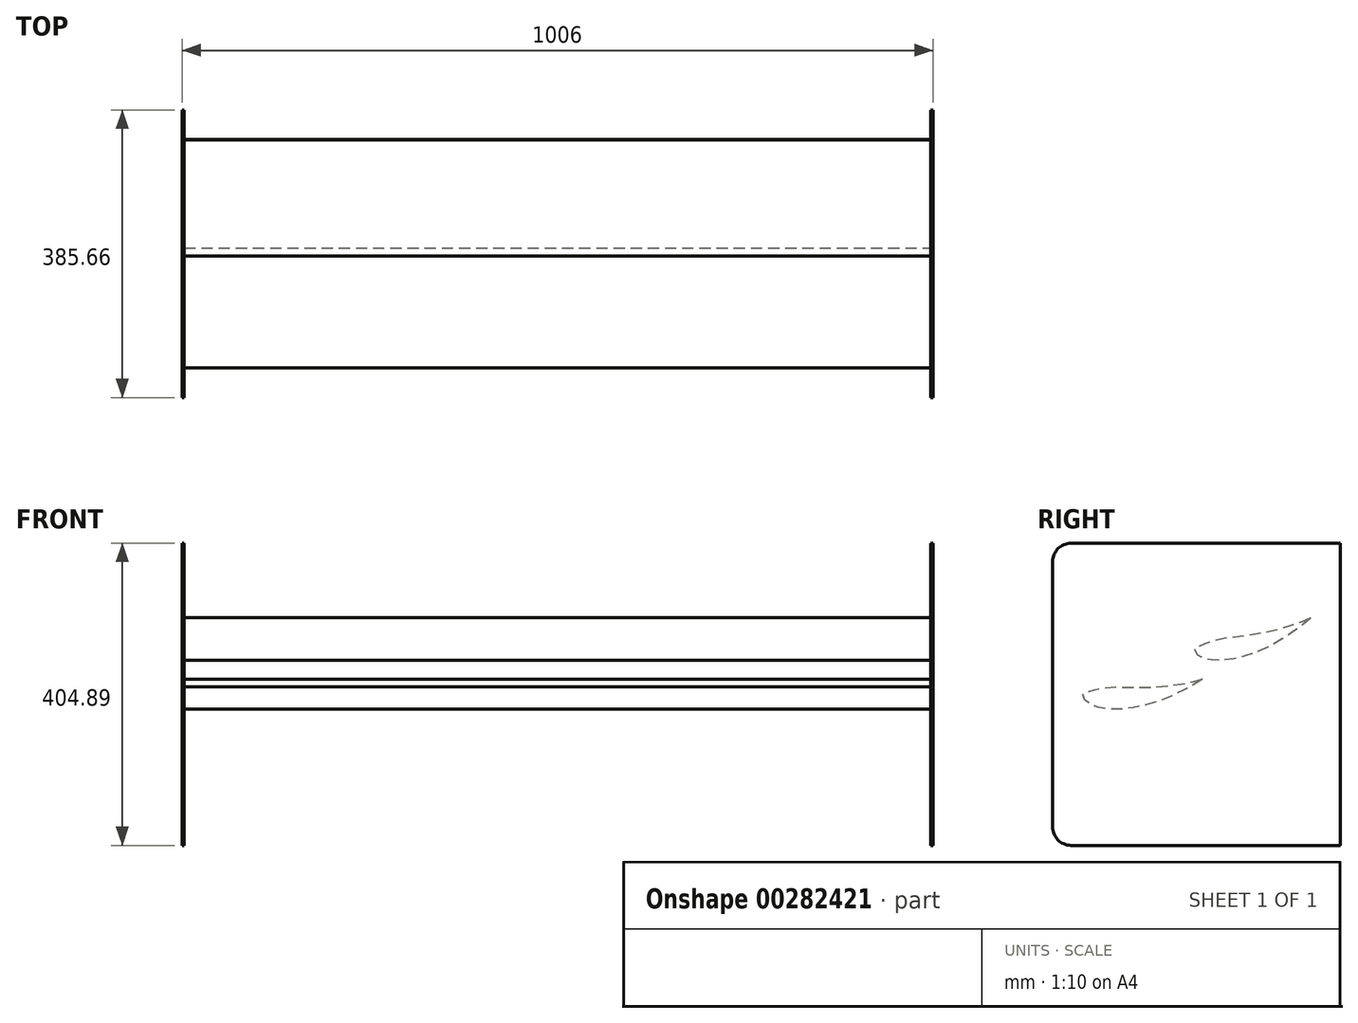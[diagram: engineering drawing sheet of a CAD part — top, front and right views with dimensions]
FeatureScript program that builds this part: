
annotation { "Feature Type Name" : "Feature", "Feature Type Description" : "" }
export const myFeature = defineFeature(function(context is Context, id is Id, definition is map)
    precondition{}
    {
        {
            var Q0;
            Q0=qCreatedBy(makeId("Right.planeOp"),FACE);
            var sketch = newSketch(context, id + "F0", { "sketchPlane" : qUnion([Q0])});
            skPoint(sketch, "E0", {"position": v(1.78, 4.63) * mm});
            skPoint(sketch, "E1", {"position": v(3.68, 7) * mm});
            skPoint(sketch, "E2", {"position": v(7.54, 10.53) * mm});
            skPoint(sketch, "E3", {"position": v(15.35, 15.89) * mm});
            skPoint(sketch, "E4", {"position": v(11.42, 13.57) * mm});
            skPoint(sketch, "E5", {"position": v(23.27, 19.3) * mm});
            skPoint(sketch, "E6", {"position": v(0, 0) * mm});
            skPoint(sketch, "E7", {"position": v(31.25, 21.57) * mm});
            skPoint(sketch, "E8", {"position": v(63.47, 24.86) * mm});
            skPoint(sketch, "E9", {"position": v(47.3, 24.4) * mm});
            skPoint(sketch, "E10", {"position": v(79.72, 23.95) * mm});
            skPoint(sketch, "E11", {"position": v(96.04, 21.74) * mm});
            skPoint(sketch, "E12", {"position": v(112.45, 17.84) * mm});
            skPoint(sketch, "E13", {"position": v(128.9, 13.21) * mm});
            skPoint(sketch, "E14", {"position": v(145.4, 7.3) * mm});
            skPoint(sketch, "E15", {"position": v(153.7, 3.82) * mm});
            skPoint(sketch, "E16", {"position": v(162, 0.24) * mm});
            skPoint(sketch, "E17", {"position": v(162, -0.24) * mm});
            skPoint(sketch, "E18", {"position": v(153.85, 0.94) * mm});
            skPoint(sketch, "E19", {"position": v(129.47, 2.44) * mm});
            skPoint(sketch, "E20", {"position": v(113.27, 2.42) * mm});
            skPoint(sketch, "E21", {"position": v(97.12, 1.47) * mm});
            skPoint(sketch, "E22", {"position": v(81.03, -0.52) * mm});
            skPoint(sketch, "E23", {"position": v(64.96, -2.92) * mm});
            skPoint(sketch, "E24", {"position": v(48.9, -5.48) * mm});
            skPoint(sketch, "E25", {"position": v(32.77, -7) * mm});
            skPoint(sketch, "E26", {"position": v(24.67, -6.94) * mm});
            skPoint(sketch, "E27", {"position": v(16.54, -6.32) * mm});
            skPoint(sketch, "E28", {"position": v(12.46, -5.77) * mm});
            skPoint(sketch, "E29", {"position": v(8.36, -4.82) * mm});
            skPoint(sketch, "E30", {"position": v(4.25, -3.66) * mm});
            skPoint(sketch, "E31", {"position": v(2.17, -2.72) * mm});
            skPoint(sketch, "E32", {"position": v(145.7, 1.72) * mm});
            skFitSpline(sketch, "E33", {"points": [v(162, 0.24) * mm, v(153.7, 3.82) * mm, v(145.4, 7.3) * mm, v(128.9, 13.21) * mm, v(112.45, 17.84) * mm, v(96.04, 21.74) * mm, v(79.72, 23.95) * mm, v(63.47, 24.86) * mm, v(47.3, 24.4) * mm, v(31.25, 21.57) * mm, v(23.27, 19.3) * mm, v(15.35, 15.89) * mm, v(11.42, 13.57) * mm, v(7.54, 10.53) * mm, v(3.68, 7) * mm, v(1.78, 4.63) * mm, v(0, 0) * mm, v(2.17, -2.72) * mm, v(4.25, -3.66) * mm, v(8.36, -4.82) * mm, v(12.46, -5.77) * mm, v(16.54, -6.32) * mm, v(24.67, -6.94) * mm, v(32.77, -7) * mm, v(48.9, -5.48) * mm, v(64.96, -2.92) * mm, v(81.03, -0.52) * mm, v(97.12, 1.47) * mm, v(113.27, 2.42) * mm, v(129.47, 2.44) * mm, v(145.7, 1.72) * mm, v(153.85, 0.94) * mm, v(162, -0.24) * mm], "startDerivative": vector(-283.63, 121.8) * mm, "endDerivative": vector(291.37, -44.72) * mm});
            skLineSegment(sketch, "E34", {"start": v(162, 0.24) * mm, "end": v(162, -0.24) * mm});
            skSolve(sketch);
        }
        {
            var Q0;
            Q0=makeQuery(id+"F0.imprint","IMPRINT",FACE,{"disambiguationData":[TD([[makeQuery(id+"F0.imprint","IMPRINT",EDGE,{"derivedFrom":sQuery(id+"F0.wireOp",EDGE,"E33")}),1.0]])]});
            extrude(context, id + "F1", {"entities" : qUnion([Q0]), "endBound" : BoundingType.SYMMETRIC, "depth" : 1000 * mm});
        }
        {
            var Q0;
            Q0=qCreatedBy(makeId("Top.planeOp"),FACE);
            var sketch = newSketch(context, id + "F2", { "sketchPlane" : qUnion([Q0])});
            skLineSegment(sketch, "E35", {"start": v(0, 0) * mm, "end": v(0, 212.68) * mm});
            skSolve(sketch);
        }
        {
            var Q0;
            Q0=makeQuery(id+"F1.opExtrude","SWEPT_BODY",BODY,{"disambiguationData":[OSD([sQuery(id+"F0.wireOp",EDGE,"E33"),sQuery(id+"F0.wireOp",EDGE,"E34")])]});
            var Q1;
            Q1=sQuery(id+"F2.wireOp",EDGE,"E35");
            transform(context, id + "F3", {"entities" : qUnion([Q0]), "transformType" : TransformType.ROTATION, "transformAxis" : qUnion([Q1]), "angle" : 180 * degree, "makeCopy" : false});
        }
        {
            var Q0;
            Q0=qCreatedBy(makeId("Top.planeOp"),FACE);
            var sketch = newSketch(context, id + "F4", { "sketchPlane" : qUnion([Q0])});
            skLineSegment(sketch, "E36", {"start": v(-76.15, 0) * mm, "end": v(75.87, 0) * mm});
            skSolve(sketch);
        }
        {
            var Q0;
            Q0=makeQuery(id+"F1.opExtrude","SWEPT_BODY",BODY,{"disambiguationData":[OSD([sQuery(id+"F0.wireOp",EDGE,"E33"),sQuery(id+"F0.wireOp",EDGE,"E34")])]});
            var Q1;
            Q1=sQuery(id+"F4.wireOp",EDGE,"E36");
            transform(context, id + "F5", {"entities" : qUnion([Q0]), "transformType" : TransformType.ROTATION, "transformAxis" : qUnion([Q1]), "angle" : 8 * degree, "makeCopy" : false});
        }
        {
            var Q0;
            Q0=makeQuery(id+"F1.opExtrude","SWEPT_BODY",BODY,{"disambiguationData":[OSD([sQuery(id+"F0.wireOp",EDGE,"E33"),sQuery(id+"F0.wireOp",EDGE,"E34")])]});
            var Q1;
            Q1=sQuery(id+"F4.wireOp",EDGE,"E36");
            transform(context, id + "F6", {"entities" : qUnion([Q0]), "transformType" : TransformType.ROTATION, "transformAxis" : qUnion([Q1]), "angle" : 8 * degree, "makeCopy" : true});
        }
        {
            var Q0;
            Q0=makeQuery(id+"F6.opPattern","COPY",BODY,{"derivedFrom":makeQuery(id+"F1.opExtrude","SWEPT_BODY",BODY,{"disambiguationData":[OSD([sQuery(id+"F0.wireOp",EDGE,"E33"),sQuery(id+"F0.wireOp",EDGE,"E34")])]}),"instanceName":"1"});
            transform(context, id + "F7", {"entities" : qUnion([Q0]), "transformType" : TransformType.TRANSLATION_3D, "dx" : 0 * mm, "dy" : 150 * mm, "dz" : 60 * mm, "makeCopy" : false});
        }
        {
            var Q0;
            Q0=makeQuery(id+"F1.opExtrude","CAP_FACE",FACE,{"disambiguationData":[OSD([sQuery(id+"F0.wireOp",EDGE,"E33"),sQuery(id+"F0.wireOp",EDGE,"E34")])],"isStart":true});
            var sketch = newSketch(context, id + "F8", { "sketchPlane" : qUnion([Q0])});
            skLineSegment(sketch, "E37.bottom", {"start": v(-40, -200) * mm, "end": v(345.66, -200) * mm});
            skLineSegment(sketch, "E37.top", {"start": v(-40, 204.89) * mm, "end": v(345.66, 204.89) * mm});
            skLineSegment(sketch, "E37.left", {"start": v(-40, -200) * mm, "end": v(-40, 204.89) * mm});
            skLineSegment(sketch, "E37.right", {"start": v(345.66, -200) * mm, "end": v(345.66, 204.89) * mm});
            skSolve(sketch);
        }
        {
            var Q0;
            Q0=makeQuery(id+"F8.imprint","IMPRINT",FACE,{"disambiguationData":[TD([[makeQuery(id+"F8.imprint","IMPRINT",EDGE,{"derivedFrom":sQuery(id+"F8.wireOp",EDGE,"E37.bottom")}),1.0]])]});
            var Q1;
            Q1=makeQuery(id+"F8.imprint","IMPRINT",FACE,{"disambiguationData":[TD([[makeQuery(id+"F8.imprint","IMPRINT",EDGE,{"derivedFrom":makeQuery(id+"F1.opExtrude","CAP_EDGE",EDGE,{"disambiguationData":[OSD([sQuery(id+"F0.wireOp",EDGE,"E33")])],"isStart":true})}),-1.0]])]});
            extrude(context, id + "F9", {"entities" : qUnion([Q0, Q1]), "depth" : 3 * mm});
        }
        {
            var Q0;
            Q0=makeQuery(id+"F9.opExtrude","SWEPT_EDGE",EDGE,{"disambiguationData":[OSD([sQuery(id+"F8.wireOp",EDGE,"E37.top"),sQuery(id+"F8.wireOp",EDGE,"E37.left")])]});
            var Q1;
            Q1=makeQuery(id+"F9.opExtrude","SWEPT_EDGE",EDGE,{"disambiguationData":[OSD([sQuery(id+"F8.wireOp",EDGE,"E37.bottom"),sQuery(id+"F8.wireOp",EDGE,"E37.left")])]});
            fillet(context, id + "F10", {"entities" : qUnion([Q0, Q1]), "radius" : 25 * mm, "tangentPropagation" : true, "allowEdgeOverflow" : false});
        }
        {
            var Q0;
            Q0=makeQuery(id+"F9.opExtrude","SWEPT_BODY",BODY,{"disambiguationData":[OSD([sQuery(id+"F8.wireOp",EDGE,"E37.bottom"),sQuery(id+"F8.wireOp",EDGE,"E37.top"),sQuery(id+"F8.wireOp",EDGE,"E37.left"),sQuery(id+"F8.wireOp",EDGE,"E37.right")])]});
            var Q1;
            Q1=qCreatedBy(makeId("Right.planeOp"),FACE);
            mirror(context, id + "F11", {"entities" : qUnion([Q0]), "mirrorPlane" : qUnion([Q1])});
        }
    });
